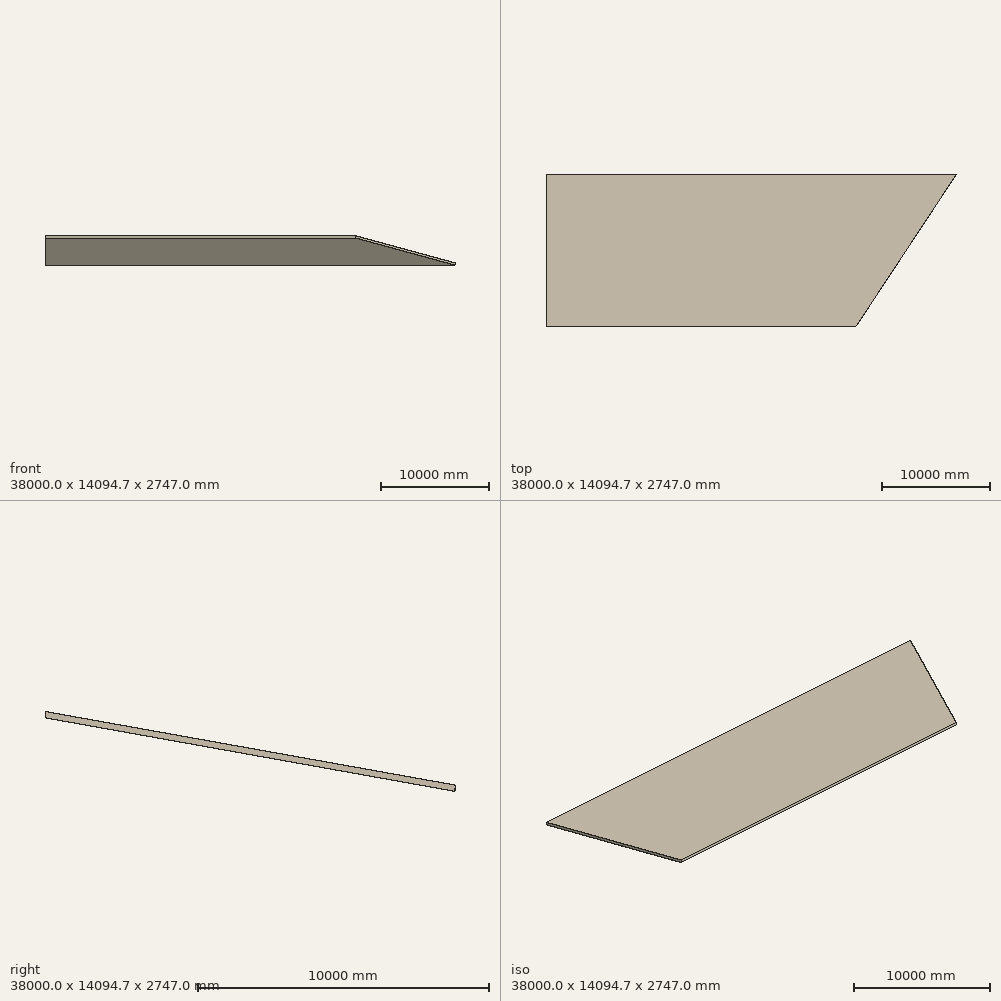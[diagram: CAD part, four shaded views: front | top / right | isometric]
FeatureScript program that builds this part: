
annotation { "Feature Type Name" : "Feature", "Feature Type Description" : "" }
export const myFeature = defineFeature(function(context is Context, id is Id, definition is map)
    precondition{}
    {
        {
            var Q0;
            Q0=qCreatedBy(makeId("Right.planeOp"),FACE);
            var sketch = newSketch(context, id + "F0", { "sketchPlane" : qUnion([Q0])});
            skLineSegment(sketch, "E0", {"start": v(0, 0) * mm, "end": v(0, 217) * mm});
            skLineSegment(sketch, "E1", {"start": v(0, 217) * mm, "end": v(14094.73, -2313) * mm});
            skLineSegment(sketch, "E2", {"start": v(14094.73, -2313) * mm, "end": v(14094.73, -2530) * mm});
            skLineSegment(sketch, "E3", {"start": v(14094.73, -2530) * mm, "end": v(0, 0) * mm});
            skSolve(sketch);
        }
        {
            var Q0;
            Q0=qSketchRegion(id+"F0",true);
            extrude(context, id + "F1", {"entities" : qUnion([Q0]), "depth" : 38000 * mm});
        }
        {
            var Q0;
            Q0=makeQuery(id+"F1.opExtrude","SWEPT_FACE",FACE,{"disambiguationData":[OSD([sQuery(id+"F0.wireOp",EDGE,"E1")])]});
            var sketch = newSketch(context, id + "F2", { "sketchPlane" : qUnion([Q0])});
            skLineSegment(sketch, "E4", {"start": v(38000, 14281.66) * mm, "end": v(26359.24, -3643.53) * mm});
            skLineSegment(sketch, "E5", {"start": v(26359.24, -3643.53) * mm, "end": v(44354.1, -3213.03) * mm});
            skLineSegment(sketch, "E6", {"start": v(44354.1, -3213.03) * mm, "end": v(43935.56, 14281.66) * mm});
            skLineSegment(sketch, "E7", {"start": v(43935.56, 14281.66) * mm, "end": v(37935.56, 14281.66) * mm});
            skSolve(sketch);
        }
        {
            var Q0;
            Q0 = qSketchRegion(id + "F2", true);
            extrude(context, id + "F3", {"entities" : qUnion([Q0]), "operationType" : NewBodyOperationType.REMOVE, "endBound" : BoundingType.THROUGH_ALL, "oppositeDirection" : true, "depth" : 25 * mm});
        }
    });
